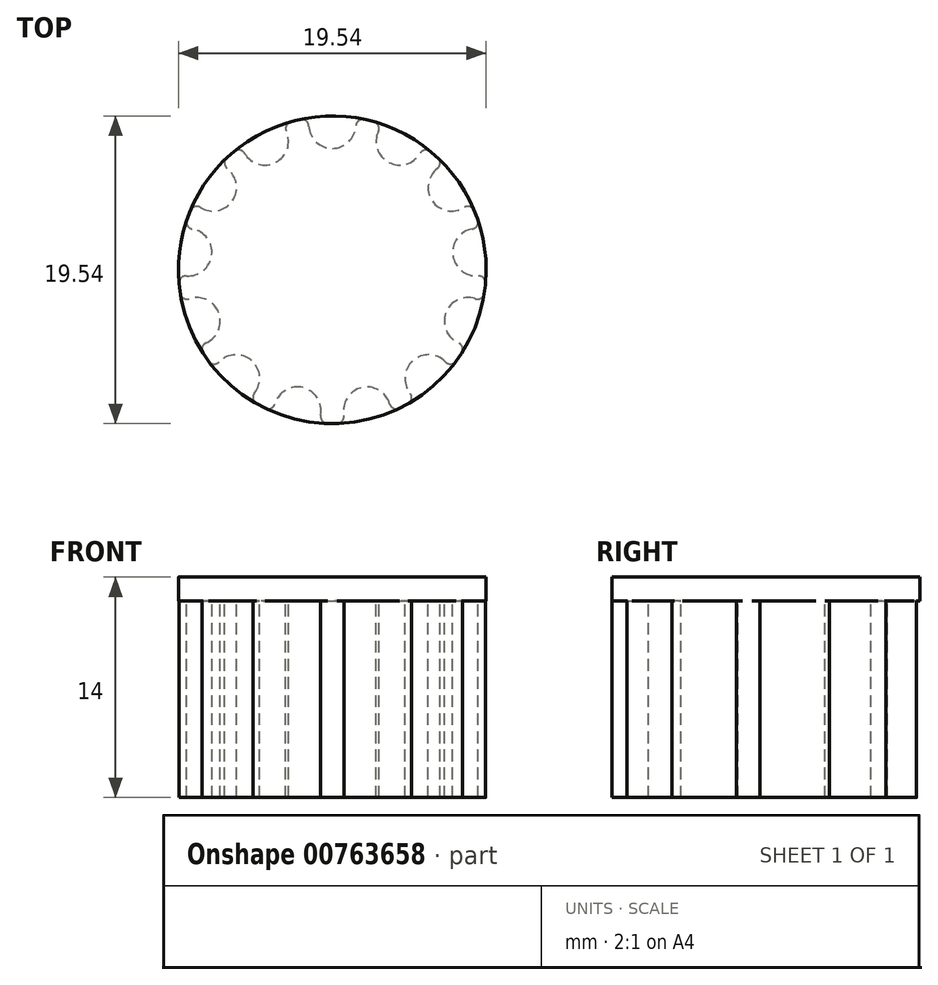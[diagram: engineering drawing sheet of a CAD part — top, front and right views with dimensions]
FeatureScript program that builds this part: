
annotation { "Feature Type Name" : "Feature", "Feature Type Description" : "" }
export const myFeature = defineFeature(function(context is Context, id is Id, definition is map)
    precondition{}
    {
        {
            assignVariable(context, id + "F0", {"name" : "Teeth", "anyValue" : 13});
        }
        {
            assignVariable(context, id + "F1", {"name" : "Width", "anyValue" : 12.5});
        }
        {
            var Q0;
            Q0=qCreatedBy(makeId("Top.planeOp"),FACE);
            var sketch = newSketch(context, id + "F2", { "sketchPlane" : qUnion([Q0])});
            skCircle(sketch, "E0", {"center": v(0, 0) * mm, "radius": 9.77 * mm});
            skSolve(sketch);
        }
        {
            var Q0;
            Q0=qSketchRegion(id+"F2",true);
            extrude(context, id + "F3", {"entities" : qUnion([Q0]), "depth" : (getVariable(context, 'Width')) * mm});
        }
        {
            var Q0;
            Q0=makeQuery(id+"F3.opExtrude","CAP_FACE",FACE,{"disambiguationData":[OSD([sQuery(id+"F2.wireOp",EDGE,"E0")])],"isStart":false});
            var sketch = newSketch(context, id + "F4", { "sketchPlane" : qUnion([Q0])});
            skCircle(sketch, "E1", {"center": v(0, 0) * mm, "radius": 7.71 * mm, "construction": true});
            skArc(sketch, "E2", {"start": v(-1.5, 9.14) * mm, "mid": v(0, 7.71) * mm, "end": v(1.5, 9.14) * mm});
            skArc(sketch, "E3", {"start": v(2.04, 9.56) * mm, "mid": v(0, 9.77) * mm, "end": v(-2.04, 9.56) * mm});
            skArc(sketch, "E4", {"start": v(-1.5, 9.14) * mm, "mid": v(-1.67, 9.47) * mm, "end": v(-2.04, 9.56) * mm});
            skArc(sketch, "E5", {"start": v(2.04, 9.56) * mm, "mid": v(1.67, 9.47) * mm, "end": v(1.5, 9.14) * mm});
            skSolve(sketch);
        }
        {
            var Q0;
            Q0=makeQuery(id+"F4.imprint","IMPRINT",FACE,{"disambiguationData":[TD([[makeQuery(id+"F4.imprint","IMPRINT",EDGE,{"derivedFrom":sQuery(id+"F4.wireOp",EDGE,"E2")}),1.0]])]});
            var Q1;
            Q1=makeQuery(id+"F3.opExtrude","CAP_FACE",FACE,{"disambiguationData":[OSD([sQuery(id+"F2.wireOp",EDGE,"E0")])],"isStart":true});
            extrude(context, id + "F5", {"entities" : qUnion([Q0]), "operationType" : NewBodyOperationType.REMOVE, "endBound" : BoundingType.UP_TO_SURFACE, "oppositeDirection" : true, "endBoundEntityFace" : qUnion([Q1]), "depth" : 25 * mm, "offsetDistance" : 25 * mm});
        }
        {
            var Q0;
            Q0=makeQuery(id+"F5.boolean.opBoolean","COPY",FACE,{"derivedFrom":makeQuery(id+"F5.opExtrude","SWEPT_FACE",FACE,{"disambiguationData":[OSD([sQuery(id+"F4.wireOp",EDGE,"E4")])]})});
            var Q1;
            Q1=makeQuery(id+"F5.boolean.opBoolean","COPY",FACE,{"derivedFrom":makeQuery(id+"F5.opExtrude","SWEPT_FACE",FACE,{"disambiguationData":[OSD([sQuery(id+"F4.wireOp",EDGE,"kHu0Iwj9-o4Cv-DRlk-4OjM-lw9Y4UkXsprA")])]})});
            var Q2;
            Q2=makeQuery(id+"F5.boolean.opBoolean","COPY",FACE,{"derivedFrom":makeQuery(id+"F5.opExtrude","SWEPT_FACE",FACE,{"disambiguationData":[OSD([sQuery(id+"F4.wireOp",EDGE,"E2")])]})});
            var Q3;
            Q3=makeQuery(id+"F5.boolean.opBoolean","COPY",FACE,{"derivedFrom":makeQuery(id+"F5.opExtrude","SWEPT_FACE",FACE,{"disambiguationData":[OSD([sQuery(id+"F4.wireOp",EDGE,"lCBZwTSR-BtAH-iuKv-YoZ4-wjcx4KIexOll")])]})});
            var Q4;
            Q4=makeQuery(id+"F5.boolean.opBoolean","COPY",FACE,{"derivedFrom":makeQuery(id+"F5.opExtrude","SWEPT_FACE",FACE,{"disambiguationData":[OSD([sQuery(id+"F4.wireOp",EDGE,"E5")])]})});
            var Q5;
            Q5=makeQuery(id+"F3.opExtrude","SWEPT_FACE",FACE,{"disambiguationData":[OSD([sQuery(id+"F2.wireOp",EDGE,"E0")])]});
            circularPattern(context, id + "F6", {"faces" : qUnion([Q0, Q1, Q2, Q3, Q4]), "axis" : qUnion([Q5]), "angle" : 360 * degree, "instanceCount" : getVariable(context, 'Teeth'), "equalSpace" : true, "patternType" : PatternType.FACE});
        }
        {
            var Q0;
            Q0=makeQuery(id+"F3.opExtrude","CAP_FACE",FACE,{"disambiguationData":[OSD([sQuery(id+"F2.wireOp",EDGE,"E0")])],"isStart":false});
            var sketch = newSketch(context, id + "F7", { "sketchPlane" : qUnion([Q0])});
            skCircle(sketch, "E6.0", {"center": v(0, 0) * mm, "radius": 9.77 * mm});
            skSolve(sketch);
        }
        {
            var Q0;
            Q0=qSketchRegion(id+"F7",true);
            extrude(context, id + "F8", {"entities" : qUnion([Q0]), "operationType" : NewBodyOperationType.ADD, "depth" : 1.5 * mm});
        }
    });
